# Revit family: 1307xxx Axios 1200 LED II
name_source: partatom
category: Lighting Fixtures
revit_build: Autodesk Revit 2018 (Build: 20170223_1515(x64)
units: mm (PartAtom-declared; Revit-internal decimal feet)

## family parameters
Always vertical = Yes
Cut with Voids When Loaded = No
Host = Wall
Light Source = Yes
OmniClass Number = 23.80.70.00
OmniClass Title = Lighting
Part Type = Normal
Room Calculation Point = No
Round Connector Dimension = Use Diameter
Shared = No

## types (2) — shared parameters
ADA compliant = N / A
Color Filter = 16777215
Dimming Lamp Color Temperature Shift = <None>
Driver Required = No
Emit from Line Length = 610 mm
Manufacturer = Astro Lighting Ltd
Manufacturer URL - Europe and Rest of World = www.astrolighting.com
Manufacturer URL - North America = us.astrolighting.com
Photometric Web File = 1307014_Axios 1200 LED II_Photometry_IES_Iss. 01.ies
Tilt Angle = 90.00°
URL = www.astrolighting.com

## per-type parameters (varying)
| type | Dimmable | Driver Included | Efficacy (lm/w) | Electrical Class | Lamp | Light Source Fixed | Location / IP Rating | Main Finish | Main Material | Power (Watts) | Product CCT | Product CRI | Product Dimensions (MM) | Product Location | Product Name | Product SKU | Product URL | Product Weight (KG) |
| CE |  |  |  | 0 |  |  |  |  | Metal - Steel |  | 2700K / 3000K | 80 / 90 |  |  |  | 1234001 |  |  |
| Astro 1307014 Axios 1200 LED II | No | Yes | 56.5 | 2 | LED | Yes | IP44 | Polished Chrome | Metal - Aluminium | 22.7 | 3000K | 80 | 1200 X 33 X 107 | Zone 2, 3 | Axios 1200 LED II | 1307014 | www.astrolighting.com/1307014 | 1.76 |

## geometry (parser evidence)
native form markers: Sweep x2
no freeform markers — native parametric forms only
